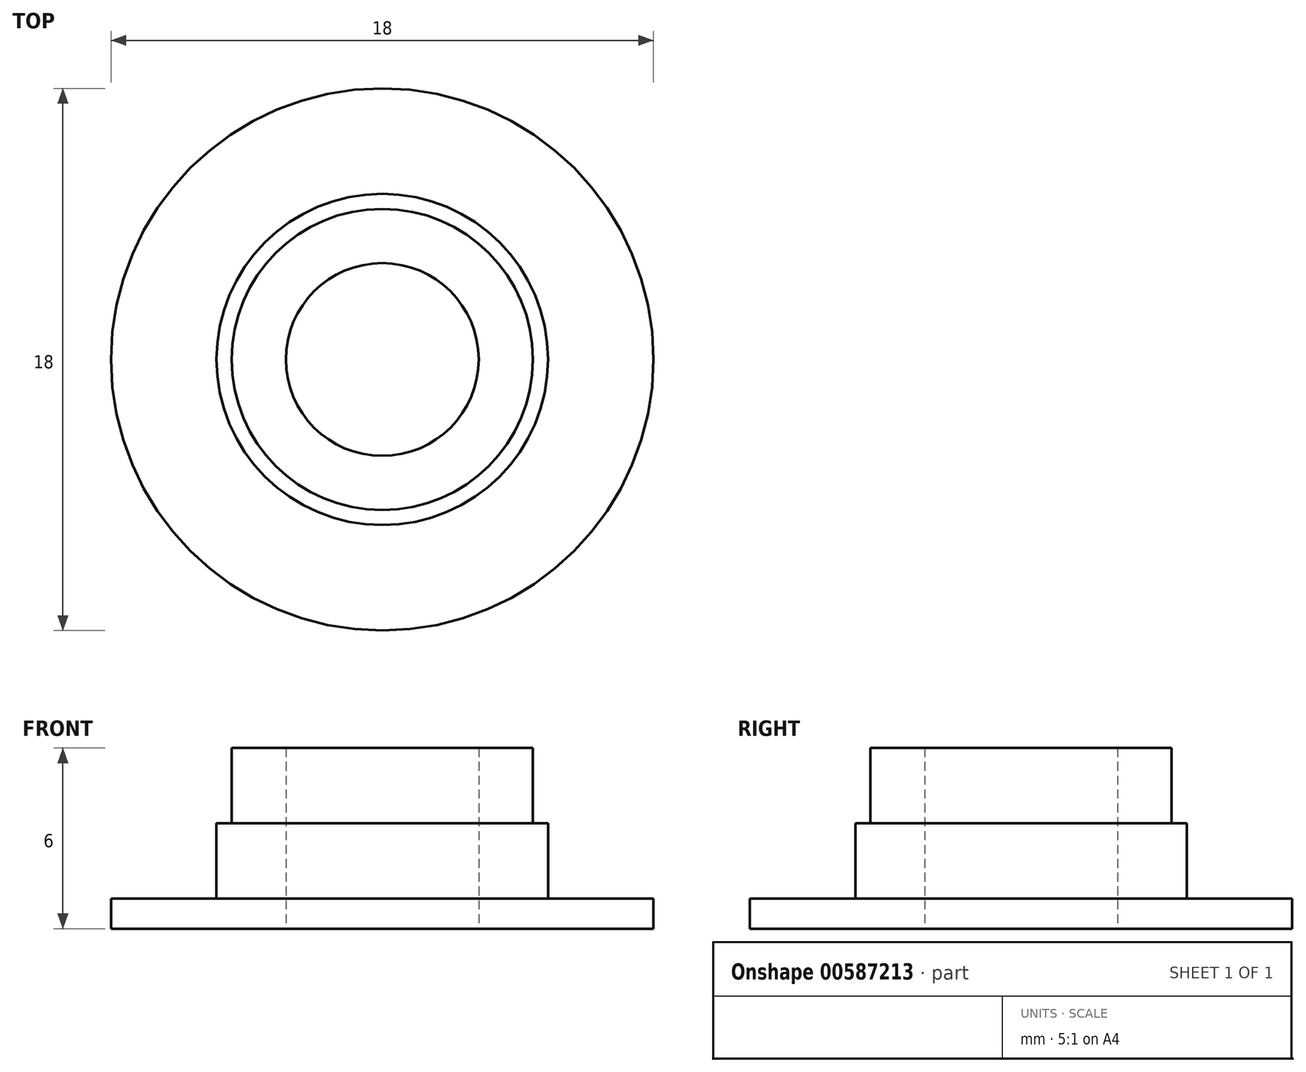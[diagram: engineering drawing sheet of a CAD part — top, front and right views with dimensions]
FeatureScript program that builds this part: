
annotation { "Feature Type Name" : "Feature", "Feature Type Description" : "" }
export const myFeature = defineFeature(function(context is Context, id is Id, definition is map)
    precondition{}
    {
        {
            var Q0;
            Q0=qCreatedBy(makeId("Front.planeOp"),FACE);
            var sketch = newSketch(context, id + "F0", { "sketchPlane" : qUnion([Q0])});
            skLineSegment(sketch, "E0.bottom", {"start": v(-9, 1) * mm, "end": v(9, 1) * mm});
            skLineSegment(sketch, "E0.top", {"start": v(-9, 0) * mm, "end": v(9, 0) * mm});
            skLineSegment(sketch, "E0.left", {"start": v(-9, 1) * mm, "end": v(-9, 0) * mm});
            skLineSegment(sketch, "E0.right", {"start": v(9, 1) * mm, "end": v(9, 0) * mm});
            skLineSegment(sketch, "E1", {"start": v(-5.5, 1) * mm, "end": v(-5.5, 3.5) * mm});
            skLineSegment(sketch, "E2", {"start": v(0, 0) * mm, "end": v(0, 42.87) * mm});
            skLineSegment(sketch, "E3", {"start": v(-3.2, 6) * mm, "end": v(-3.2, 0) * mm});
            skLineSegment(sketch, "E4", {"start": v(3.2, 6) * mm, "end": v(3.2, 0) * mm});
            skLineSegment(sketch, "E5", {"start": v(-5.5, 3.5) * mm, "end": v(5.5, 3.5) * mm});
            skLineSegment(sketch, "E6", {"start": v(5.5, 3.5) * mm, "end": v(5.5, 1) * mm});
            skLineSegment(sketch, "E7", {"start": v(-5, 3.5) * mm, "end": v(-5, 6) * mm});
            skLineSegment(sketch, "E8", {"start": v(5, 3.5) * mm, "end": v(5, 6) * mm});
            skLineSegment(sketch, "E9", {"start": v(-5, 6) * mm, "end": v(5, 6) * mm});
            skSolve(sketch);
        }
        {
            var Q0;
            {var subQ1=sQuery(id+"F0.wireOp",EDGE,"E1");Q0=makeQuery(id+"F0.imprint","IMPRINT",FACE,{"disambiguationData":[TD([[makeQuery(id+"F0.imprint","IMPRINT",EDGE,{"derivedFrom":subQ1}),-1.0]])]});}
            var Q1;
            {var subQ5=sQuery(id+"F0.wireOp",EDGE,"E7");Q1=makeQuery(id+"F0.imprint","IMPRINT",FACE,{"disambiguationData":[TD([[makeQuery(id+"F0.imprint","IMPRINT",EDGE,{"derivedFrom":subQ5}),-1.0]])]});}
            var Q2;
            {var subQ0=sQuery(id+"F0.wireOp",EDGE,"E0.left");Q2=makeQuery(id+"F0.imprint","IMPRINT",FACE,{"disambiguationData":[TD([[makeQuery(id+"F0.imprint","IMPRINT",EDGE,{"derivedFrom":subQ0}),1.0]])]});}
            var Q3;
            Q3=sQuery(id+"F0.wireOp",EDGE,"E2");
            revolve(context, id + "F1", {"entities" : qUnion([Q0, Q1, Q2]), "axis" : qUnion([Q3]), "revolveType" : RevolveType.FULL});
        }
    });
